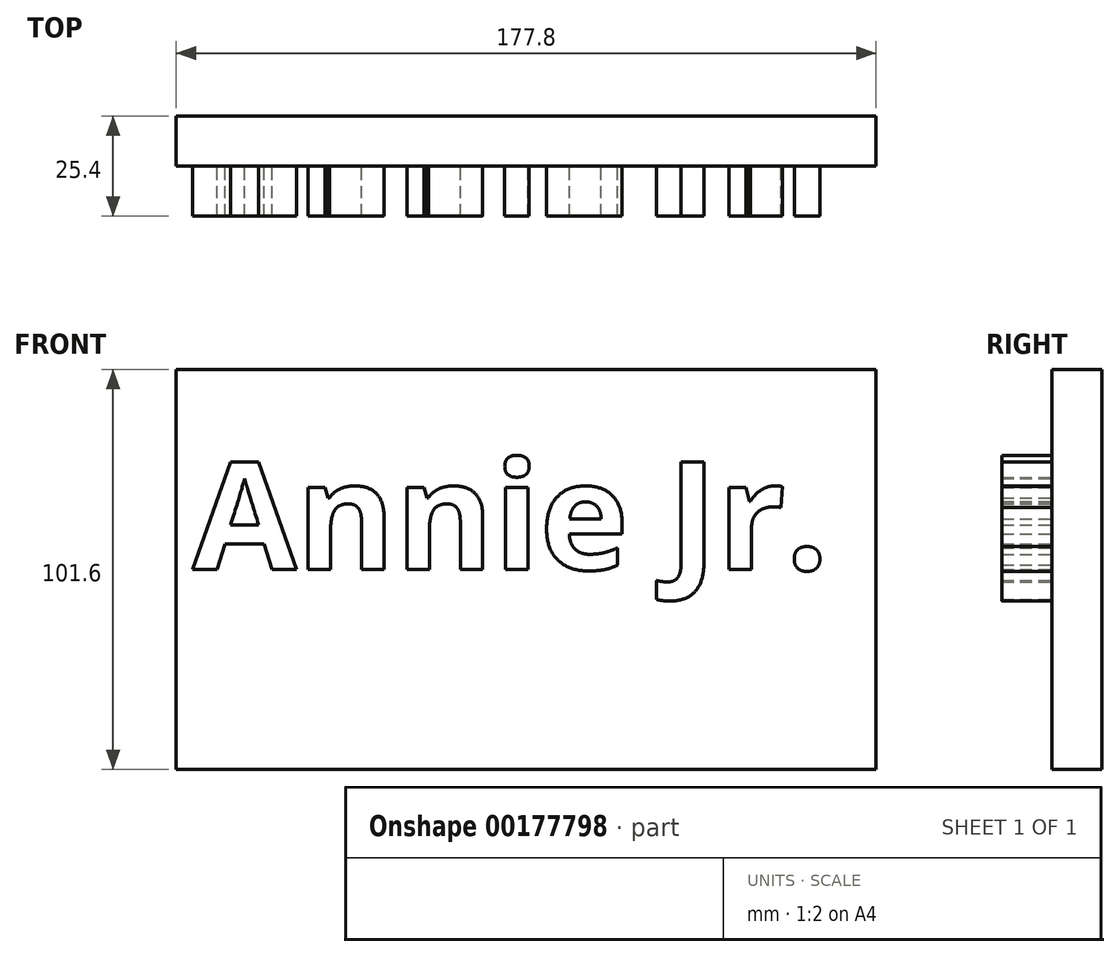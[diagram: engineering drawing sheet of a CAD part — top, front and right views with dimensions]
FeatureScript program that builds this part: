
annotation { "Feature Type Name" : "Feature", "Feature Type Description" : "" }
export const myFeature = defineFeature(function(context is Context, id is Id, definition is map)
    precondition{}
    {
        {
            var Q0;
            Q0=qCreatedBy(makeId("Front.planeOp"),FACE);
            var sketch = newSketch(context, id + "F0", { "sketchPlane" : qUnion([Q0])});
            skLineSegment(sketch, "E0.bottom", {"start": v(88.9, 50.8) * mm, "end": v(-88.9, 50.8) * mm});
            skLineSegment(sketch, "E0.top", {"start": v(88.9, -50.8) * mm, "end": v(-88.9, -50.8) * mm});
            skLineSegment(sketch, "E0.left", {"start": v(88.9, 50.8) * mm, "end": v(88.9, -50.8) * mm});
            skLineSegment(sketch, "E0.right", {"start": v(-88.9, 50.8) * mm, "end": v(-88.9, -50.8) * mm});
            skPoint(sketch, "E0.middle", {"position": v(0, 0) * mm});
            skSolve(sketch);
        }
        {
            var Q0;
            Q0 = qSketchRegion(id + "F0", true);
            extrude(context, id + "F2", {"entities" : qUnion([Q0]), "depth" : 12.7 * mm});
        }
        {
            var Q0;
            Q0=makeQuery(id+"F2.opExtrude","CAP_FACE",FACE,{"disambiguationData":[OSD([sQuery(id+"F0.wireOp",EDGE,"E0.bottom"),sQuery(id+"F0.wireOp",EDGE,"E0.top"),sQuery(id+"F0.wireOp",EDGE,"E0.left"),sQuery(id+"F0.wireOp",EDGE,"E0.right")])],"isStart":false});
            var sketch = newSketch(context, id + "F1", { "sketchPlane" : qUnion([Q0])});
            skSolve(sketch);
        }
        {
            var Q0;
            Q0=makeQuery(id+"F1.imprint","IMPRINT",FACE,{"disambiguationData":[TD([[makeQuery(id+"F1.imprint","IMPRINT",EDGE,{"derivedFrom":makeQuery(id+"F2.opExtrude","CAP_EDGE",EDGE,{"disambiguationData":[OSD([sQuery(id+"F0.wireOp",EDGE,"E0.bottom")])],"isStart":false})}),1.0]])]});
            var sketch = newSketch(context, id + "F3", { "sketchPlane" : qUnion([Q0])});
            skText(sketch, "E1", { "text": "Annie Jr.", "fontName": "OpenSans-Bold.ttf"});
            const initialGuessFygtFlD2pwO1FsrVU_1  = {"E1": [-0.0847, 0, 1, 0, 0.02749]};
            skSetInitialGuess(sketch, initialGuessFygtFlD2pwO1FsrVU_1);
            skSolve(sketch);
        }
        {
            var Q0;
            Q0 = qSketchRegion(id + "F3", true);
            extrude(context, id + "F4", {"entities" : qUnion([Q0]), "operationType" : NewBodyOperationType.ADD, "depth" : 12.7 * mm});
        }
    });
